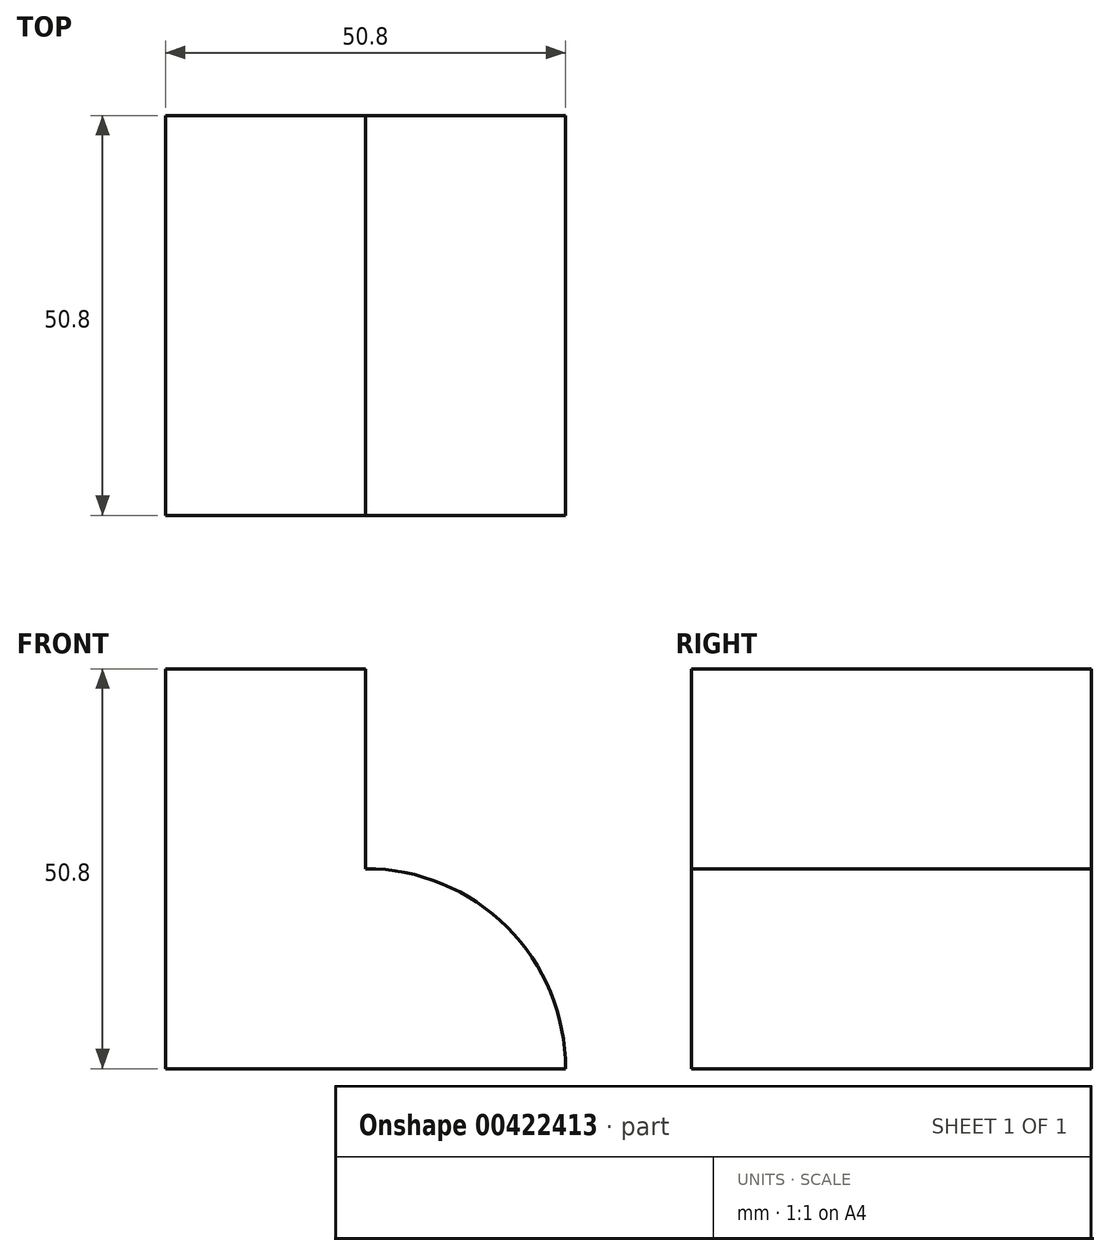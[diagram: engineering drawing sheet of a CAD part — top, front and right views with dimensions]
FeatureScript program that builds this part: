
annotation { "Feature Type Name" : "Feature", "Feature Type Description" : "" }
export const myFeature = defineFeature(function(context is Context, id is Id, definition is map)
    precondition{}
    {
        {
            var Q0;
            Q0=qCreatedBy(makeId("Front.planeOp"),FACE);
            var sketch = newSketch(context, id + "F0", { "sketchPlane" : qUnion([Q0])});
            skLineSegment(sketch, "E0", {"start": v(0, 0) * mm, "end": v(-50.8, 0) * mm});
            skLineSegment(sketch, "E1", {"start": v(-50.8, 50.8) * mm, "end": v(-50.8, 0) * mm});
            skLineSegment(sketch, "E2", {"start": v(-25.4, 50.8) * mm, "end": v(-50.8, 50.8) * mm});
            skLineSegment(sketch, "E3", {"start": v(-25.4, 50.8) * mm, "end": v(-25.4, 25.4) * mm});
            skArc(sketch, "E4", {"start": v(0, 0) * mm, "mid": v(-7.42, 17.98) * mm, "end": v(-25.4, 25.4) * mm});
            skSolve(sketch);
        }
        {
            var Q0;
            Q0 = qSketchRegion(id + "F0", true);
            extrude(context, id + "F1", {"entities" : qUnion([Q0]), "depth" : 50.8 * mm});
        }
    });
